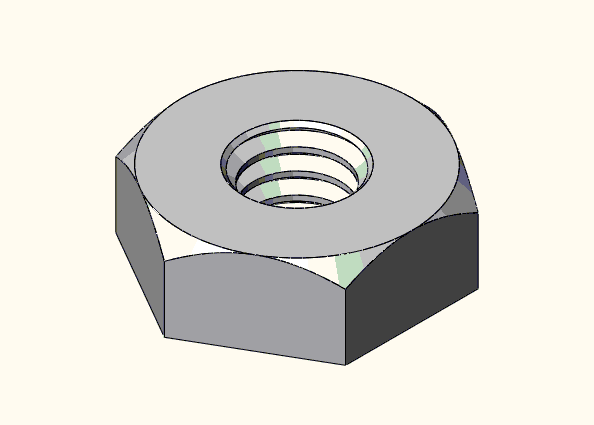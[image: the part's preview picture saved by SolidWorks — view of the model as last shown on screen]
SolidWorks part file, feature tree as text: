
SOLIDWORKS PART (.sldprt)
format: sldprt  version: not decoded by parser v0  size: 160,768 bytes
history: native  units: mm
features: sketch x3, cut_revolve x2, material x1, extrude x1, pattern_linear x1, chamfer x1 (+14 scaffold rows collapsed)
feature tree (23):
  scaffold x14  (default folders/planes/origin — collapsed)
  material  "Material <not specified>"
  sketch  "Sketch1"  dims[Hex Flats=~8.73125mm]
  extrude  "Extrude1"  Depth=3.175mm Height=3.175mm
  sketch  "Sketch3"  dims[c1.D1=~0.569483mm c2.D1=45.0deg c2.D2=~8.73125mm]
  cut_revolve  "Cut-Revolve2"  Angle=360deg
  sketch  "Sketch2"  dims[c1.D1=1.524mm c1.D2=~0.039688mm c1.D3=~0.079375mm c1.D4=0.3175mm c1.D5=~0.099129mm c2.D5=60.0deg c2.D1=~0.142294mm c3.D1=60.0deg c3.Pitch=~0.79375mm c3.Major Dia.=4.1656mm c3.D4=~0.079375mm c3.D5=~0.099219mm c3.D2=~0.198437mm]
  cut_revolve  "Cut-Revolve1"  Angle=360deg
  pattern_linear  "LPattern2"  Count1=5 Count2=1 Spacing1=0.79375mm Spacing2=50mm
  chamfer  "Chamfer1"  Distance=0.396875mm Angle=45deg hex flats=14.2748mm hex flats/2=7.366mm
decode coverage: 8 of 8 modeling features carry decoded parameters
note: ~ marks probable driven/reference dimensions
note: suppression state not decoded; provenance and decode notes live in map.json
